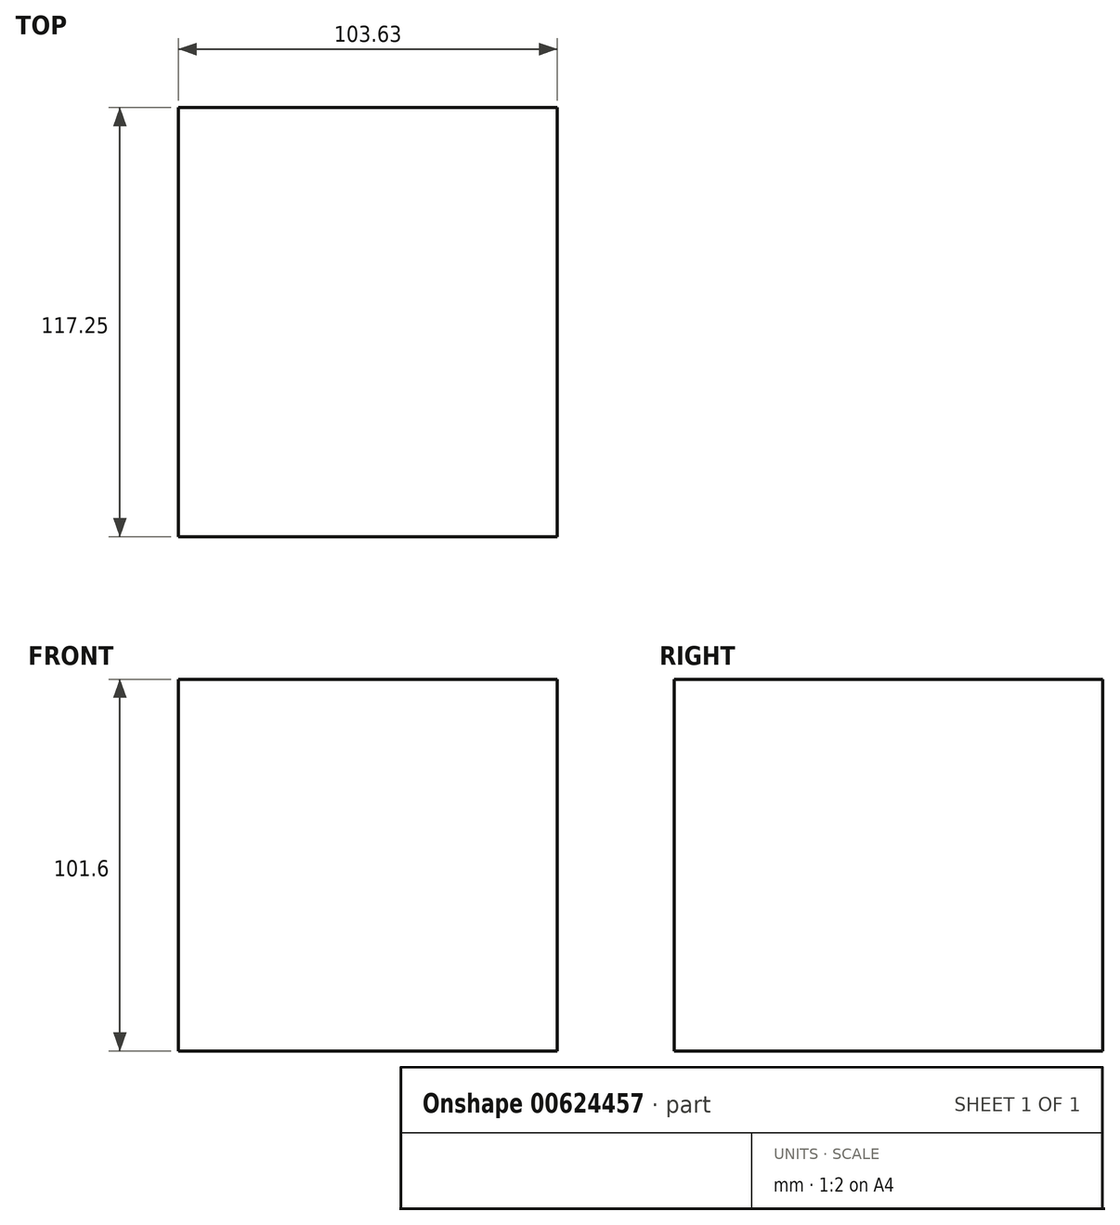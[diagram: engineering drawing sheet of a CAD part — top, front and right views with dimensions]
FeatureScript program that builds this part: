
annotation { "Feature Type Name" : "Feature", "Feature Type Description" : "" }
export const myFeature = defineFeature(function(context is Context, id is Id, definition is map)
    precondition{}
    {
        {
            var Q0;
            Q0=qCreatedBy(makeId("Top.planeOp"),FACE);
            var sketch = newSketch(context, id + "F0", { "sketchPlane" : qUnion([Q0])});
            skLineSegment(sketch, "E0.bottom", {"start": v(-53.7, 64.55) * mm, "end": v(49.93, 64.55) * mm});
            skLineSegment(sketch, "E0.top", {"start": v(-53.7, -52.7) * mm, "end": v(49.93, -52.7) * mm});
            skLineSegment(sketch, "E0.left", {"start": v(-53.7, 64.55) * mm, "end": v(-53.7, -52.7) * mm});
            skLineSegment(sketch, "E0.right", {"start": v(49.93, 64.55) * mm, "end": v(49.93, -52.7) * mm});
            skSolve(sketch);
        }
        {
            var Q0;
            Q0 = qSketchRegion(id + "F0", true);
            extrude(context, id + "F1", {"entities" : qUnion([Q0]), "depth" : 101.6 * mm, "offsetDistance" : 25.4 * mm});
        }
    });
